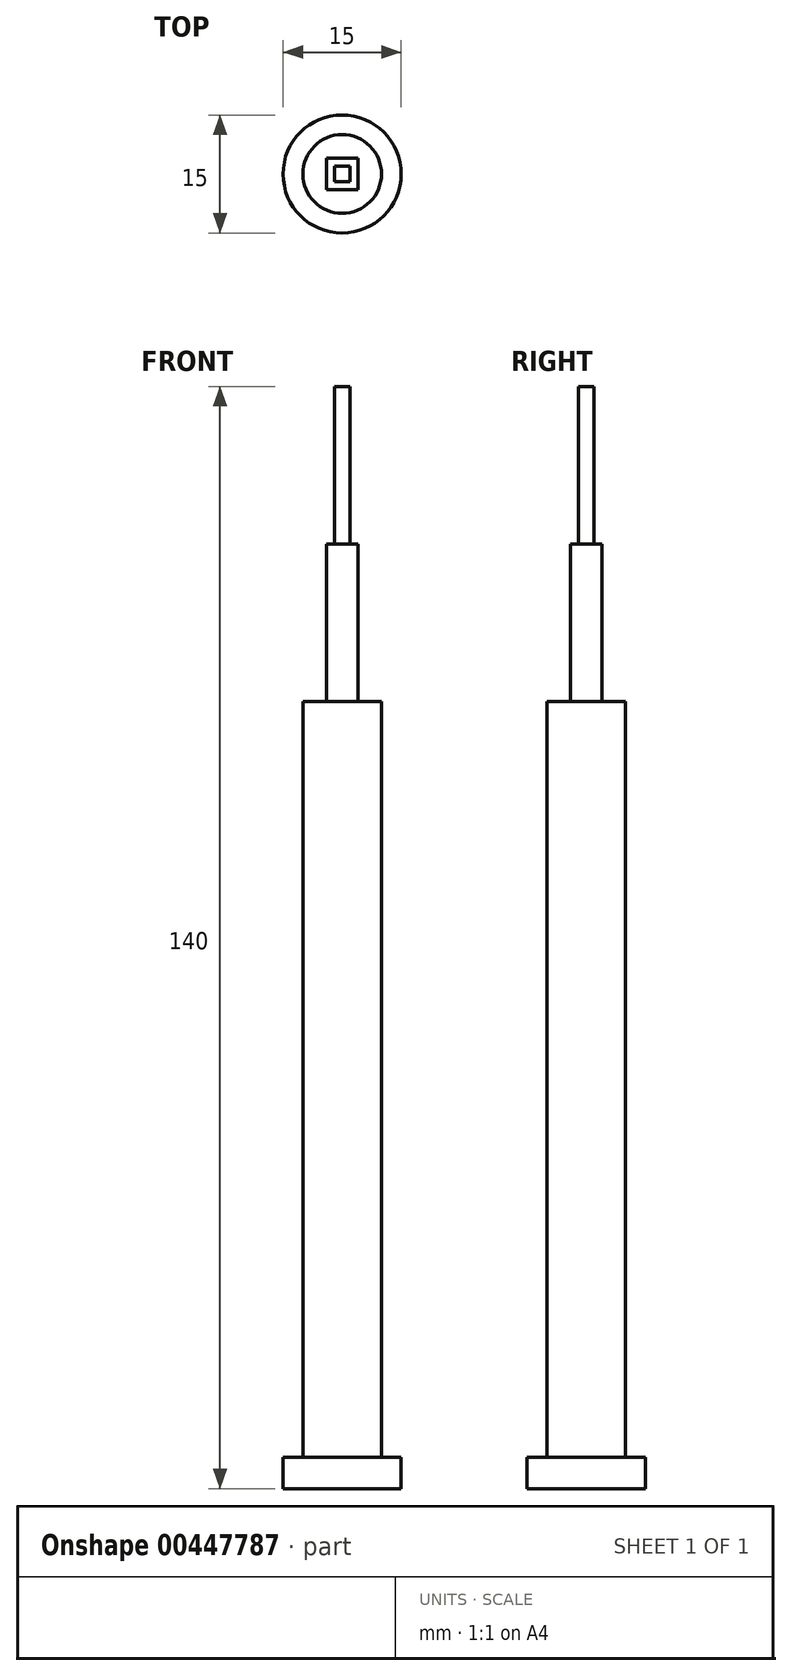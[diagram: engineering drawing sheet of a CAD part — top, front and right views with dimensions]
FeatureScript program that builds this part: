
annotation { "Feature Type Name" : "Feature", "Feature Type Description" : "" }
export const myFeature = defineFeature(function(context is Context, id is Id, definition is map)
    precondition{}
    {
        {
            var Q0;
            Q0=qCreatedBy(makeId("Top.planeOp"),FACE);
            var sketch = newSketch(context, id + "F0", { "sketchPlane" : qUnion([Q0])});
            skCircle(sketch, "E0", {"center": v(0, 0) * mm, "radius": 7.5 * mm});
            skSolve(sketch);
        }
        {
            var Q0;
            Q0=qSketchRegion(id+"F0",true);
            extrude(context, id + "F1", {"entities" : qUnion([Q0]), "depth" : 4 * mm});
        }
        {
            var Q0;
            Q0=qCreatedBy(makeId("Top.planeOp"),FACE);
            var sketch = newSketch(context, id + "F2", { "sketchPlane" : qUnion([Q0])});
            skCircle(sketch, "E1", {"center": v(0, 0) * mm, "radius": 5 * mm});
            skSolve(sketch);
        }
        {
            var Q0;
            Q0=qSketchRegion(id+"F2",true);
            extrude(context, id + "F3", {"entities" : qUnion([Q0]), "operationType" : NewBodyOperationType.ADD, "depth" : 100 * mm});
        }
        {
            var Q0;
            Q0=makeQuery(id+"F3.opExtrude","CAP_FACE",FACE,{"disambiguationData":[OSD([sQuery(id+"F2.wireOp",EDGE,"E1")])],"isStart":false});
            var sketch = newSketch(context, id + "F4", { "sketchPlane" : qUnion([Q0])});
            skLineSegment(sketch, "E2.bottom", {"start": v(-2, 2) * mm, "end": v(2, 2) * mm});
            skLineSegment(sketch, "E2.top", {"start": v(-2, -2) * mm, "end": v(2, -2) * mm});
            skLineSegment(sketch, "E2.left", {"start": v(-2, 2) * mm, "end": v(-2, -2) * mm});
            skLineSegment(sketch, "E2.right", {"start": v(2, 2) * mm, "end": v(2, -2) * mm});
            skSolve(sketch);
        }
        {
            var Q0;
            Q0=makeQuery(id+"F4.imprint","IMPRINT",FACE,{"disambiguationData":[TD([[makeQuery(id+"F4.imprint","IMPRINT",EDGE,{"derivedFrom":sQuery(id+"F4.wireOp",EDGE,"E2.bottom")}),-1.0]])]});
            extrude(context, id + "F5", {"entities" : qUnion([Q0]), "operationType" : NewBodyOperationType.ADD, "depth" : 20 * mm});
        }
        {
            var Q0;
            Q0=makeQuery(id+"F5.opExtrude","CAP_FACE",FACE,{"disambiguationData":[OSD([sQuery(id+"F4.wireOp",EDGE,"E2.bottom"),sQuery(id+"F4.wireOp",EDGE,"E2.top"),sQuery(id+"F4.wireOp",EDGE,"E2.left"),sQuery(id+"F4.wireOp",EDGE,"E2.right")])],"isStart":false});
            var sketch = newSketch(context, id + "F6", { "sketchPlane" : qUnion([Q0])});
            skLineSegment(sketch, "E3.bottom", {"start": v(-1, 1) * mm, "end": v(1, 1) * mm});
            skLineSegment(sketch, "E3.top", {"start": v(-1, -1) * mm, "end": v(1, -1) * mm});
            skLineSegment(sketch, "E3.left", {"start": v(-1, 1) * mm, "end": v(-1, -1) * mm});
            skLineSegment(sketch, "E3.right", {"start": v(1, 1) * mm, "end": v(1, -1) * mm});
            skSolve(sketch);
        }
        {
            var Q0;
            Q0 = qSketchRegion(id + "F6", true);
            extrude(context, id + "F7", {"entities" : qUnion([Q0]), "operationType" : NewBodyOperationType.ADD, "depth" : 20 * mm});
        }
    });
